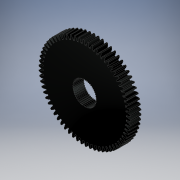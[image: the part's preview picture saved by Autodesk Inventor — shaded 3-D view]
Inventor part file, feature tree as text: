
AUTODESK INVENTOR PART (.ipt)
format: ipt  version: 2017 (Build 210142000, 142)  size: 1,056,256 bytes
history: native  units: in
note: dims shown in document units (in); Inventor stores cm internally (conversion verified against a paired STEP export)
features: sketch x6, extrude x5, pattern_circular x2, plane x1
ambient origin geometry x8: Origin, YZ Plane, XZ Plane, XY Plane, X Axis, Y Axis, Z Axis, Center Point
bodies: Solid1 (feature_tree)
feature tree (14):
  sketch  "Sketch2"  dims[d0=1.2992in d1=0.1374in]
  extrude  "Extrusion1"  Depth=0.1374in
  extrude  "Extrusion3"  Depth=0.0591in
  pattern_circular  "Circular Pattern1"  [2 undecoded]
  extrude  "Extrusion12"  Depth=0.3937in TaperAngle=360.0deg
  extrude  "Extrusion19"  Depth=0.3937in
  extrude  "Extrusion21"  Depth=0.3937in
  pattern_circular  "Circular Pattern3"  [2 undecoded]
  plane  "Work Plane17"
  sketch  "Sketch4"  dims[d6=0.2222in d7=0.0591in]
  sketch  "Sketch5"  dims[d8=0.1631in]
  sketch  "Sketch24"  dims[d9=0.0094in]
  sketch  "Sketch47"  dims[d10=1.4567in]
  sketch  "Sketch49"  dims[d12=0.1575in d13=0.0in d16=0.1969in d17=0.0in d18=25.9843in d19=360.0deg d61=0.0787in d62=0.3009in d64=0.0039in d121=1.3386in d122=2.6772in d123=0.3937in d124=0.0in d183=0.3268in d184=0.3937in d185=0.0in d193=0.0247in d195=0.3268in d196=0.1752in d197=0.3937in d198=0.0in d199=19.685in d200=360.0deg d202=-0.0787in]
note: 4 required parameter values undecoded (feature->parameter linkage not recoverable at this tier; creation-order binding heuristic only, values carry confidence <= 0.55)
